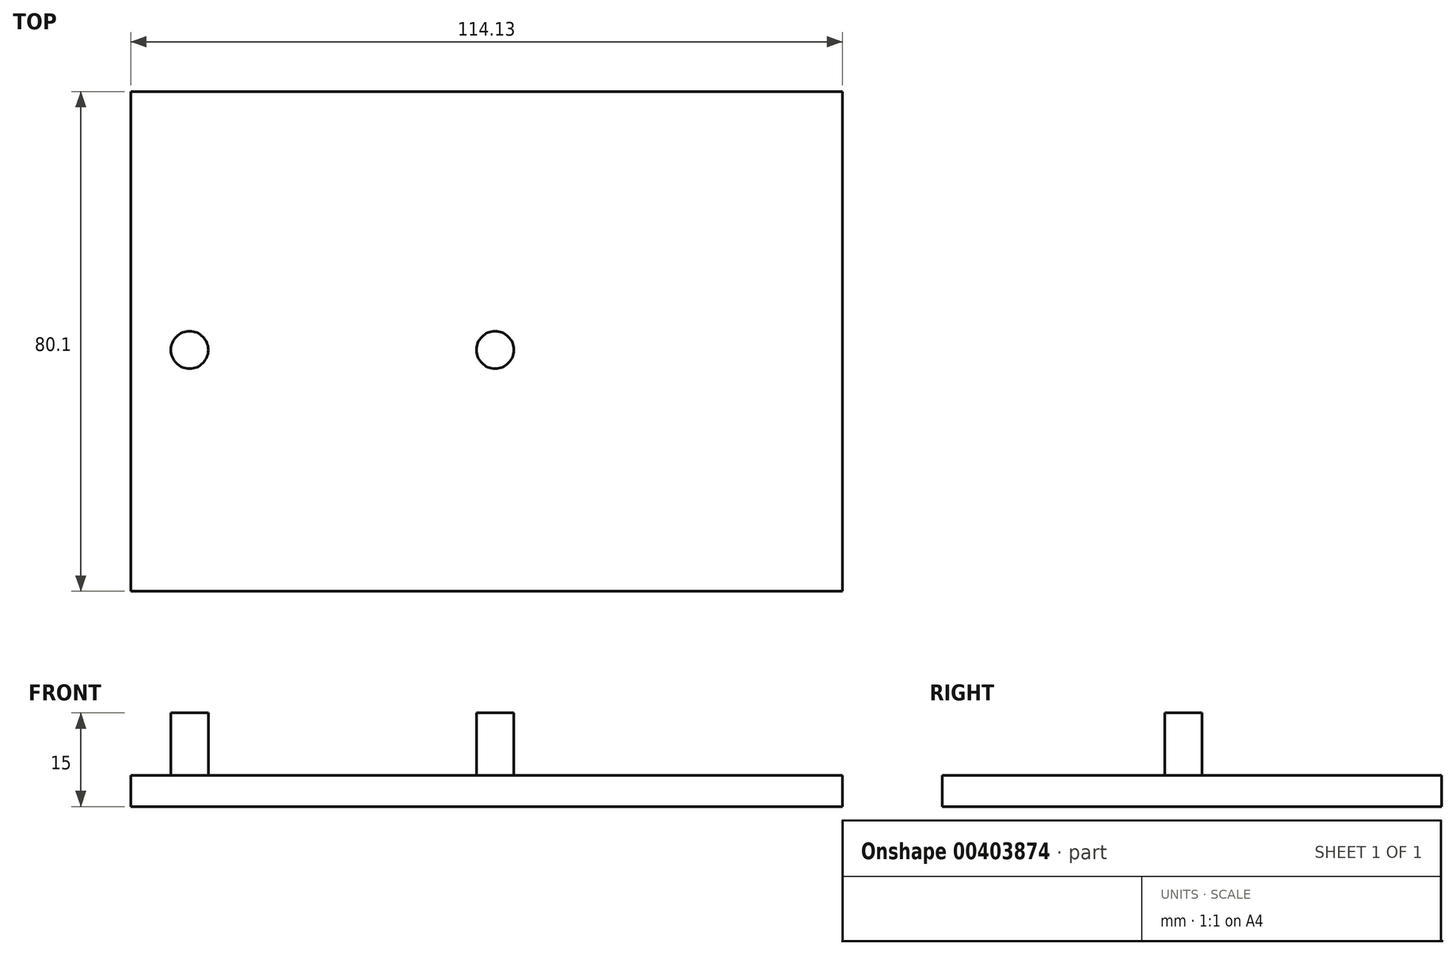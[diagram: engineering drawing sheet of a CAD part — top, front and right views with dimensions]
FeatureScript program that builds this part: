
annotation { "Feature Type Name" : "Feature", "Feature Type Description" : "" }
export const myFeature = defineFeature(function(context is Context, id is Id, definition is map)
    precondition{}
    {
        {
            var Q0;
            Q0=qCreatedBy(makeId("Top.planeOp"),FACE);
            var sketch = newSketch(context, id + "F0", { "sketchPlane" : qUnion([Q0])});
            skLineSegment(sketch, "E0.bottom", {"start": v(70, -60) * mm, "end": v(-70, -60) * mm});
            skLineSegment(sketch, "E0.top", {"start": v(70, 60) * mm, "end": v(-70, 60) * mm});
            skLineSegment(sketch, "E0.left", {"start": v(70, -60) * mm, "end": v(70, 60) * mm});
            skLineSegment(sketch, "E0.right", {"start": v(-70, -60) * mm, "end": v(-70, 60) * mm});
            skPoint(sketch, "E0.middle", {"position": v(0, 0) * mm});
            skCircle(sketch, "E1", {"center": v(0, 0) * mm, "radius": 3 * mm});
            skLineSegment(sketch, "E2", {"start": v(0, 0) * mm, "end": v(-49, 0) * mm});
            skCircle(sketch, "E3", {"center": v(-49, 0) * mm, "radius": 3 * mm});
            skSolve(sketch);
        }
        {
            var Q0;
            Q0=makeQuery(id+"F0.imprint","IMPRINT",FACE,{"disambiguationData":[TD([[makeQuery(id+"F0.imprint","IMPRINT",EDGE,{"derivedFrom":sQuery(id+"F0.wireOp",EDGE,"E3")}),1.0]])]});
            var Q1;
            Q1=makeQuery(id+"F0.imprint","IMPRINT",FACE,{"disambiguationData":[TD([[makeQuery(id+"F0.imprint","IMPRINT",EDGE,{"derivedFrom":sQuery(id+"F0.wireOp",EDGE,"E1")}),1.0]])]});
            extrude(context, id + "F1", {"entities" : qUnion([Q0, Q1]), "depth" : 10 * mm});
        }
        {
            var Q0;
            Q0=qCreatedBy(makeId("Top.planeOp"),FACE);
            var sketch = newSketch(context, id + "F2", { "sketchPlane" : qUnion([Q0])});
            skLineSegment(sketch, "E4.bottom", {"start": v(-58.44, 41.41) * mm, "end": v(55.69, 41.41) * mm});
            skLineSegment(sketch, "E4.top", {"start": v(-58.44, -38.7) * mm, "end": v(55.69, -38.7) * mm});
            skLineSegment(sketch, "E4.left", {"start": v(-58.44, 41.41) * mm, "end": v(-58.44, -38.7) * mm});
            skLineSegment(sketch, "E4.right", {"start": v(55.69, 41.41) * mm, "end": v(55.69, -38.7) * mm});
            skSolve(sketch);
        }
        {
            var Q0;
            Q0 = qSketchRegion(id + "F2", true);
            extrude(context, id + "F3", {"entities" : qUnion([Q0]), "oppositeDirection" : true, "depth" : 5 * mm});
        }
    });
